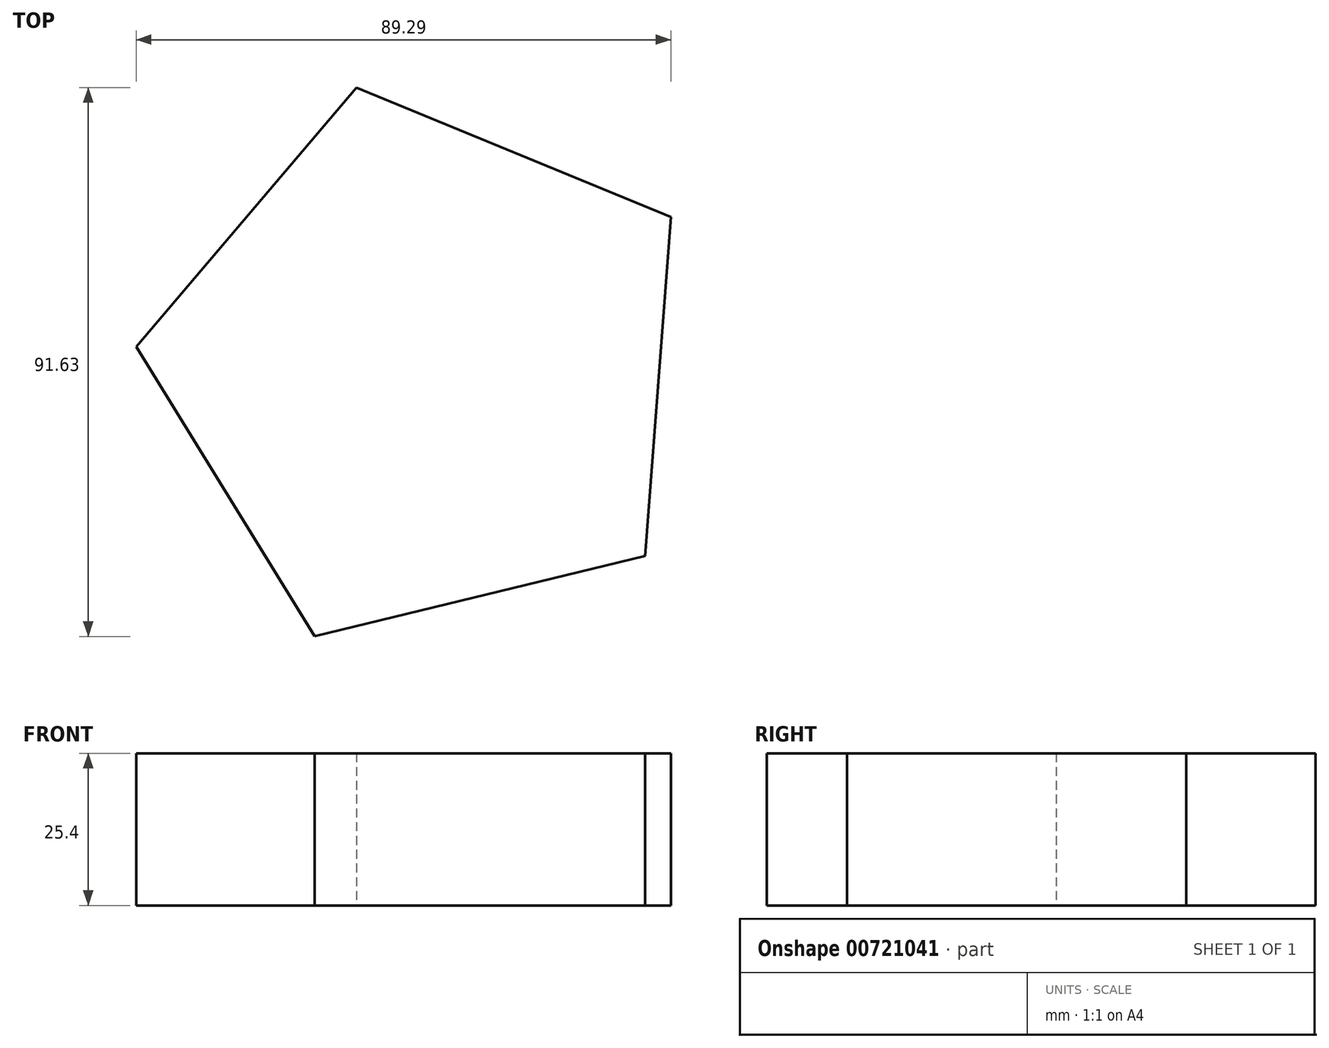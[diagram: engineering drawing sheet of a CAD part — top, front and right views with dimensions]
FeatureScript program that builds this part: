
annotation { "Feature Type Name" : "Feature", "Feature Type Description" : "" }
export const myFeature = defineFeature(function(context is Context, id is Id, definition is map)
    precondition{}
    {
        {
            var Q0;
            Q0=qCreatedBy(makeId("Top.planeOp"),FACE);
            var sketch = newSketch(context, id + "F0", { "sketchPlane" : qUnion([Q0])});
            skCircle(sketch, "E0.cCircle", {"center": v(-28.65, -16.1) * mm, "radius": 39.08 * mm, "construction": true});
            skLineSegment(sketch, "E0.0", {"start": v(-76.82, -12.45) * mm, "end": v(-40.05, 30.84) * mm});
            skLineSegment(sketch, "E0.1", {"start": v(-40.05, 30.84) * mm, "end": v(12.47, 9.25) * mm});
            skLineSegment(sketch, "E0.2", {"start": v(12.47, 9.25) * mm, "end": v(8.17, -47.38) * mm});
            skLineSegment(sketch, "E0.3", {"start": v(8.17, -47.38) * mm, "end": v(-47.01, -60.79) * mm});
            skLineSegment(sketch, "E0.4", {"start": v(-47.01, -60.79) * mm, "end": v(-76.82, -12.45) * mm});
            skPoint(sketch, "E0.0.midPoint", {"position": v(-58.43, 9.2) * mm});
            skSolve(sketch);
        }
        {
            var Q0;
            Q0 = qSketchRegion(id + "F0", true);
            extrude(context, id + "F1", {"entities" : qUnion([Q0]), "depth" : 25.4 * mm, "offsetDistance" : 25.4 * mm});
        }
    });
